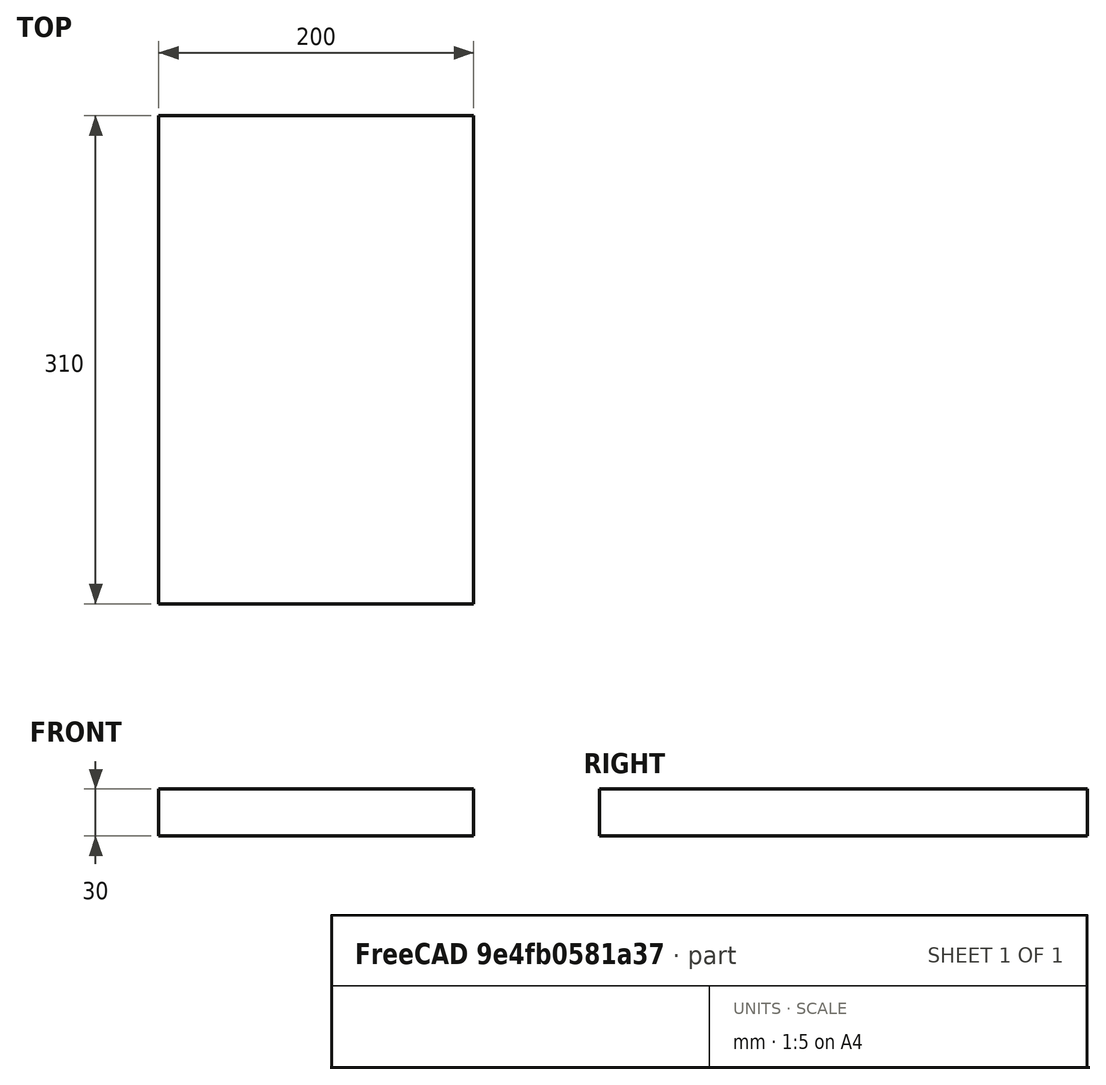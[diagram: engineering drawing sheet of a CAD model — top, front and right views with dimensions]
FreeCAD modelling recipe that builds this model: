
FCSTD DOCUMENT  (FreeCAD 1.0R39319 (Git))
Label: base-plate-small
License: All rights reserved
LicenseURL: https://en.wikipedia.org/wiki/All_rights_reserved
objects: Sketcher::SketchObject×1, PartDesign::Pad×1, PartDesign::Body×1
note: 6 computed .brp shape members not serialized (recipe doc carries the construction recipe); baked Part::Feature solids carry a one-line shape summary decoded from their .brp

FEATURE [Sketcher::SketchObject] Sketch
  ArcFitTolerance = 1e-06
  AttachmentSupport = -> [XY_Plane]
  FullyConstrained = true
  MakeInternals = false
  MapMode = 5
  sketch-geometry (4):
    g0: LineSegment StartX=0 StartY=0 StartZ=0 EndX=200 EndY=0 EndZ=0
    g1: LineSegment StartX=200 StartY=0 StartZ=0 EndX=200 EndY=310 EndZ=0
    g2: LineSegment StartX=200 StartY=310 StartZ=0 EndX=0 EndY=310 EndZ=0
    g3: LineSegment StartX=0 StartY=310 StartZ=0 EndX=0 EndY=0 EndZ=0
  constraints (11):
    c: Coincident(g0,g1)
    c: Coincident(g1,g2)
    c: Coincident(g2,g3)
    c: Coincident(g3,g0)
    c: Horizontal(g0)
    c: Horizontal(g2)
    c: Vertical(g1)
    c: Vertical(g3)
    c: Distance(g1,g3) = 200
    c: Distance(g0,g2) = 310
    c: Coincident(g0,g-1)
FEATURE [PartDesign::Pad] Pad
  Direction = (0,0,1)
  Length = 30
  Length2 = 10
  Profile = -> Sketch
  ReferenceAxis = -> Sketch [N_Axis]
  Refine = true
  Suppressed = false
  Type = 0
FEATURE [PartDesign::Body] Body
  AllowCompound = false
  Group = -> [Sketch,Pad]
  Origin = -> Origin
  Tip = -> Pad
